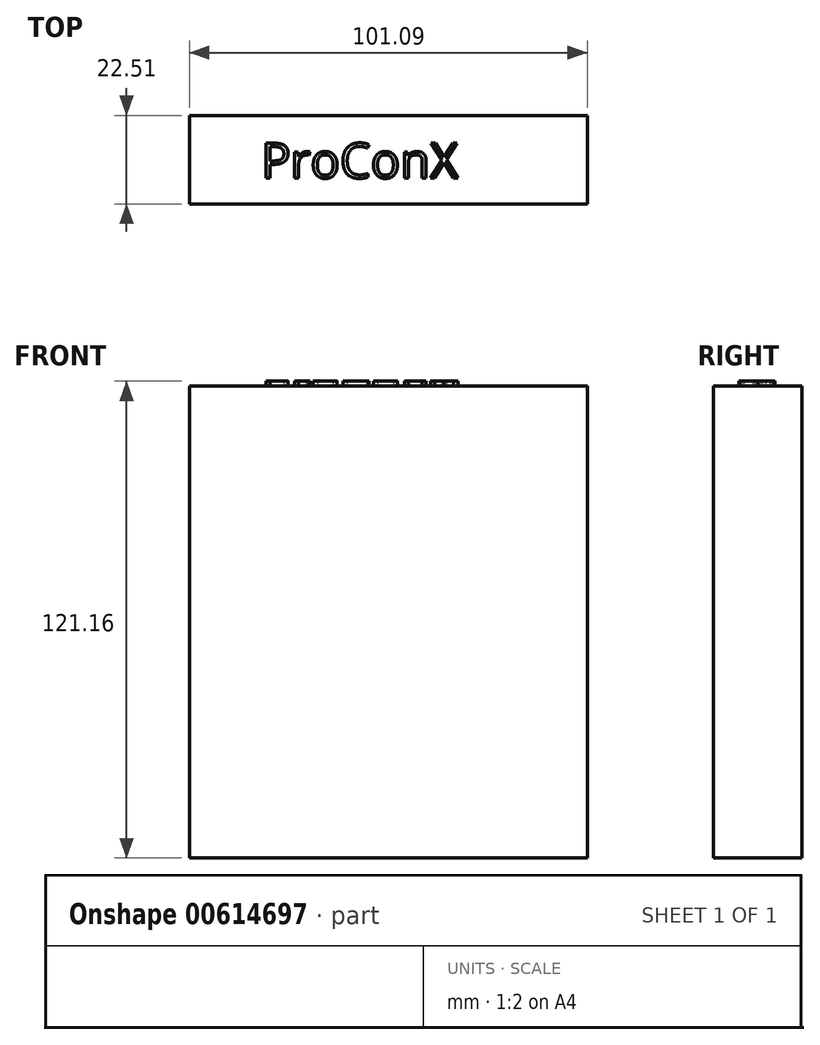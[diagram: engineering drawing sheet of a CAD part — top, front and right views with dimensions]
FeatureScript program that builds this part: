
annotation { "Feature Type Name" : "Feature", "Feature Type Description" : "" }
export const myFeature = defineFeature(function(context is Context, id is Id, definition is map)
    precondition{}
    {
        {
            var Q0;
            Q0=qCreatedBy(makeId("Top.planeOp"),FACE);
            var sketch = newSketch(context, id + "F0", { "sketchPlane" : qUnion([Q0])});
            skLineSegment(sketch, "E0.bottom", {"start": v(-42.3, 11.77) * mm, "end": v(58.8, 11.77) * mm});
            skLineSegment(sketch, "E0.top", {"start": v(-42.3, -10.74) * mm, "end": v(58.8, -10.74) * mm});
            skLineSegment(sketch, "E0.left", {"start": v(-42.3, 11.77) * mm, "end": v(-42.3, -10.74) * mm});
            skLineSegment(sketch, "E0.right", {"start": v(58.8, 11.77) * mm, "end": v(58.8, -10.74) * mm});
            skSolve(sketch);
        }
        {
            var Q0;
            Q0=makeQuery(id+"F0.imprint","IMPRINT",FACE,{"disambiguationData":[TD([[makeQuery(id+"F0.imprint","IMPRINT",EDGE,{"derivedFrom":sQuery(id+"F0.wireOp",EDGE,"E0.bottom")}),-1.0]])]});
            extrude(context, id + "F1", {"entities" : qUnion([Q0]), "depth" : 119.89 * mm, "offsetDistance" : 25.4 * mm});
        }
        {
            var Q0;
            Q0=makeQuery(id+"F1.opExtrude","CAP_FACE",FACE,{"disambiguationData":[OSD([sQuery(id+"F0.wireOp",EDGE,"E0.bottom"),sQuery(id+"F0.wireOp",EDGE,"E0.top"),sQuery(id+"F0.wireOp",EDGE,"E0.left"),sQuery(id+"F0.wireOp",EDGE,"E0.right")])],"isStart":false});
            var sketch = newSketch(context, id + "F2", { "sketchPlane" : qUnion([Q0])});
            skText(sketch, "E1", { "text": "ProConX", "fontName": "OpenSans-Regular.ttf"});
            const initialGuessF2  = {"E1": [-0.02408, -0.00413, 1, 0, 0.00892]};
            skSetInitialGuess(sketch, initialGuessF2);
            skSolve(sketch);
        }
        {
            var Q0;
            Q0 = qSketchRegion(id + "F2", true);
            extrude(context, id + "F3", {"entities" : qUnion([Q0]), "operationType" : NewBodyOperationType.ADD, "depth" : 1.27 * mm, "offsetDistance" : 25.4 * mm});
        }
    });
